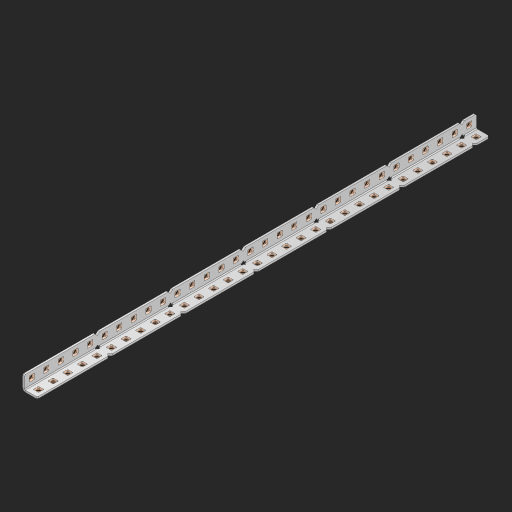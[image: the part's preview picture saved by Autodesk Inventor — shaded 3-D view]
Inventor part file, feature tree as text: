
AUTODESK INVENTOR PART (.ipt)
format: ipt  version: 2023 (Build 270158000, 158)  size: 1,061,376 bytes
history: native  units: in
note: dims shown in document units (in); Inventor stores cm internally (conversion verified against a paired STEP export)
features: other x68, extrude x63, sheet_metal_op x8, sketch x5, pattern_linear x1, mirror x1, chamfer x1
ambient origin geometry x8: Origin, YZ Plane, XZ Plane, XY Plane, X Axis, Y Axis, Z Axis, Center Point
bodies: Solid1 (feature_tree), Body (feature_tree)
feature tree (147):
  sheet_metal_op  "Flanges"
  sheet_metal_op  "Body Pattern"
  other  "Arc Length"
  pattern_linear  "Notch Pattern"  Spacing1=0.125in  [1 undecoded]
  other  "Diagonal Plane"
  mirror  "Everything Mirrored"
  chamfer  "End Chamfer"
  sketch  "Sketch1"  dims[d0=0.5in]
  other  "Plate1"
  sketch  "Sketch2"  dims[d1=15.5in]
  other  "Plate2"
  sheet_metal_op  "Bend1"
  sheet_metal_op  "Corner1"
  sketch  "Sketch8"  dims[d2=0.0625in]
  sketch  "Sketch9"  dims[d3=0.0625in]
  other  "Srf91"
  sheet_metal_op  "Body Pattern Sketch"
  other  "Srf92"
  sketch  "Sketch13"  dims[d4=0.0312in d5=0.125in d6=0.0625in d7=0.5in d8=90.0deg d9=0.0312in d10=0.25in d11=0.0625in d12=0.0625in d49=0.182in d50=0.02in d52=0.25in d53=0.0625in d54=0.0in d55=0.172in d56=1.0in d57=0.0in d85=0.1473in d86=0.1782in d89=0.0625in d90=0.0in d91=0.04in d92=0.0491in d95=2.5in d96=0.04in d97=0.25in d98=45.0deg d123=0.204in d126=0.0491in d127=0.1473in d128=0.08in d129=0.04in d130=2.5in d131=12.2047in d133=0.5in d134=0.3937in d136=1.0in]
  other  "Srf856"
  other  "Srf857"
  other  "Srf858"
  other  "Srf859"
  other  "Srf860"
  other  "Srf861"
  other  "Srf1275"
  other  "Srf1276"
  other  "Srf1278"
  other  "Srf1279"
  other  "Srf1280"
  other  "Srf1281"
  other  "Srf1282"
  other  "Srf1283"
  other  "Srf1383"
  other  "Srf1384"
  other  "Srf1385"
  other  "Srf1386"
  other  "Srf1387"
  other  "Srf1388"
  other  "Srf1389"
  other  "Srf1390"
  other  "Srf1391"
  other  "Srf1392"
  other  "Srf1393"
  other  "Srf1394"
  other  "Srf1395"
  other  "Srf1396"
  other  "Srf1397"
  other  "Srf1398"
  other  "Srf1399"
  other  "Srf1400"
  other  "Srf1401"
  other  "Srf1402"
  other  "Srf1403"
  other  "Srf1404"
  other  "Srf1405"
  other  "Srf1406"
  other  "Srf1475"
  other  "Srf1476"
  other  "Srf1477"
  other  "Srf1478"
  other  "Srf1479"
  other  "Srf1480"
  other  "Srf1481"
  other  "Srf1482"
  other  "Srf1483"
  other  "Srf1484"
  other  "Srf1485"
  other  "Srf1486"
  other  "Srf1487"
  other  "Srf1488"
  other  "Srf1489"
  other  "Srf1490"
  other  "Srf1491"
  other  "Srf1492"
  other  "Srf1493"
  other  "Srf1494"
  other  "Srf1495"
  other  "Srf1496"
  other  "Srf1497"
  other  "Srf1498"
  sheet_metal_op  "Body Stamp"
  sheet_metal_op  "Body Circle"
  sheet_metal_op  "Notch"
  extrude  "ExtrusionSrf92"  Depth=0.0625in
  extrude  "ExtrusionSrf856"  Depth=0.5in TaperAngle=90.0deg
  extrude  "ExtrusionSrf857"  Depth=0.25in
  extrude  "ExtrusionSrf858"  Depth=0.0625in
  extrude  "ExtrusionSrf859"  Depth=0.0625in
  extrude  "ExtrusionSrf860"  Depth=0.3937in
  extrude  "ExtrusionSrf861"  Depth=0.02in
  extrude  "ExtrusionSrf1275"  Depth=0.25in
  extrude  "ExtrusionSrf1276"  Depth=0.0625in
  extrude  "ExtrusionSrf1277"  TaperAngle=0.0deg  [1 undecoded]
  extrude  "ExtrusionSrf1278"  Depth=0.3937in
  extrude  "ExtrusionSrf1279"  Depth=0.3937in TaperAngle=0.0deg
  extrude  "ExtrusionSrf1280"  Depth=0.3937in
  extrude  "ExtrusionSrf1281"  Depth=0.3937in
  extrude  "ExtrusionSrf1282"  Depth=0.0625in
  extrude  "ExtrusionSrf1383"  Depth=0.3937in TaperAngle=0.0deg
  extrude  "ExtrusionSrf1384"  Depth=0.3937in
  extrude  "ExtrusionSrf1385"  Depth=0.25in TaperAngle=45.0deg
  extrude  "ExtrusionSrf1386"  Depth=0.3937in
  extrude  "ExtrusionSrf1387"  Depth=0.3937in
  extrude  "ExtrusionSrf1388"  Depth=0.3937in
  extrude  "ExtrusionSrf1389"  Depth=0.3937in
  extrude  "ExtrusionSrf1390"  Depth=0.3937in
  extrude  "ExtrusionSrf1391"  Depth=0.3937in
  extrude  "ExtrusionSrf1392"  Depth=0.3937in
  extrude  "ExtrusionSrf1393"  Depth=0.5in
  extrude  "ExtrusionSrf1394"  [1 undecoded]
  extrude  "ExtrusionSrf1395"  [1 undecoded]
  extrude  "ExtrusionSrf1396"  [1 undecoded]
  extrude  "ExtrusionSrf1397"  [1 undecoded]
  extrude  "ExtrusionSrf1398"  [1 undecoded]
  extrude  "ExtrusionSrf1399"  [1 undecoded]
  extrude  "ExtrusionSrf1400"  [1 undecoded]
  extrude  "ExtrusionSrf1401"  [1 undecoded]
  extrude  "ExtrusionSrf1402"  [1 undecoded]
  extrude  "ExtrusionSrf1403"  [1 undecoded]
  extrude  "ExtrusionSrf1404"  [1 undecoded]
  extrude  "ExtrusionSrf1405"  [1 undecoded]
  extrude  "ExtrusionSrf1406"  [1 undecoded]
  extrude  "ExtrusionSrf1475"  [1 undecoded]
  extrude  "ExtrusionSrf1476"  [1 undecoded]
  extrude  "ExtrusionSrf1477"  [1 undecoded]
  extrude  "ExtrusionSrf1478"  [1 undecoded]
  extrude  "ExtrusionSrf1479"  [1 undecoded]
  extrude  "ExtrusionSrf1480"  [1 undecoded]
  extrude  "ExtrusionSrf1481"  [1 undecoded]
  extrude  "ExtrusionSrf1482"  [1 undecoded]
  extrude  "ExtrusionSrf1483"  [1 undecoded]
  extrude  "ExtrusionSrf1484"  [1 undecoded]
  extrude  "ExtrusionSrf1485"  [1 undecoded]
  extrude  "ExtrusionSrf1486"  [1 undecoded]
  extrude  "ExtrusionSrf1487"  [1 undecoded]
  extrude  "ExtrusionSrf1488"  [1 undecoded]
  extrude  "ExtrusionSrf1489"  [1 undecoded]
  extrude  "ExtrusionSrf1490"  [1 undecoded]
  extrude  "ExtrusionSrf1491"  [1 undecoded]
  extrude  "ExtrusionSrf1492"  [1 undecoded]
  extrude  "ExtrusionSrf1493"  [1 undecoded]
  extrude  "ExtrusionSrf1494"  [1 undecoded]
  extrude  "ExtrusionSrf1495"  [1 undecoded]
  extrude  "ExtrusionSrf1496"  [1 undecoded]
  extrude  "ExtrusionSrf1497"  [1 undecoded]
  extrude  "ExtrusionSrf1498"  [1 undecoded]
note: 39 required parameter values undecoded (feature->parameter linkage not recoverable at this tier; creation-order binding heuristic only, values carry confidence <= 0.55)
